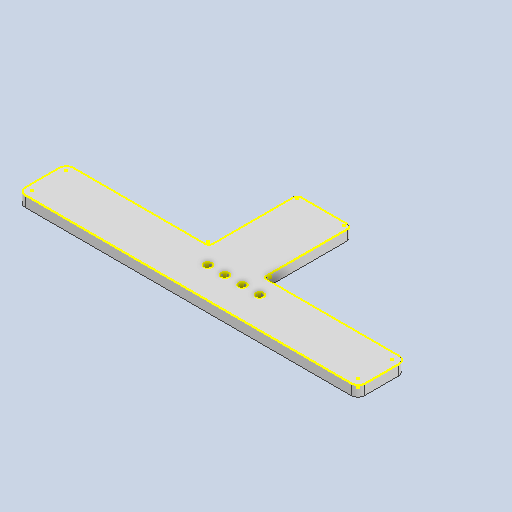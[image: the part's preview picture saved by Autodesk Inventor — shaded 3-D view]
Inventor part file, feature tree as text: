
AUTODESK INVENTOR PART (.ipt)
format: ipt  version: 2023.5 (Build 275446000, 446)  size: 289,792 bytes
history: native  units: mm
features: other x6, reference x4, extrude x3, fillet x2, sketch x1, projected_geometry x1
ambient origin geometry x8: Origin, YZ Plane, XZ Plane, XY Plane, X Axis, Y Axis, Z Axis, Center Point
bodies: Body1 (feature_tree)
feature tree (17):
  other  "Bryła1"
  extrude  "Wyciągnięcie proste1"  Depth=50.0mm
  fillet  "Zaokrąglenie1"  Radius=7.0mm
  extrude  "Wyciągnięcie proste2"  Depth=1.6mm TaperAngle=0.0deg
  extrude  "Wyciągnięcie proste3"  Depth=1.0mm
  fillet  "Zaokrąglenie3"  Radius=14.0mm
  sketch  "Szkic2"
  reference  "Odniesienie1"
  reference  "Odniesienie2"
  reference  "Odniesienie3"
  reference  "Odniesienie4"
  projected_geometry  "Pętla rzutowana2"
  parser-record x1  (decoder bookkeeping rows leaked as tree rows — omitted from the tree; the rows remain in map.json)
  other  "byk_v3.iam"
  other  "servo_mini_1370hd_cos:2"
  other  "servo_mini_1370hd_cos:1"
  other  "podstawa:1"
note: 1 file-system path scrubbed to <path> (originals preserved in map.json)
